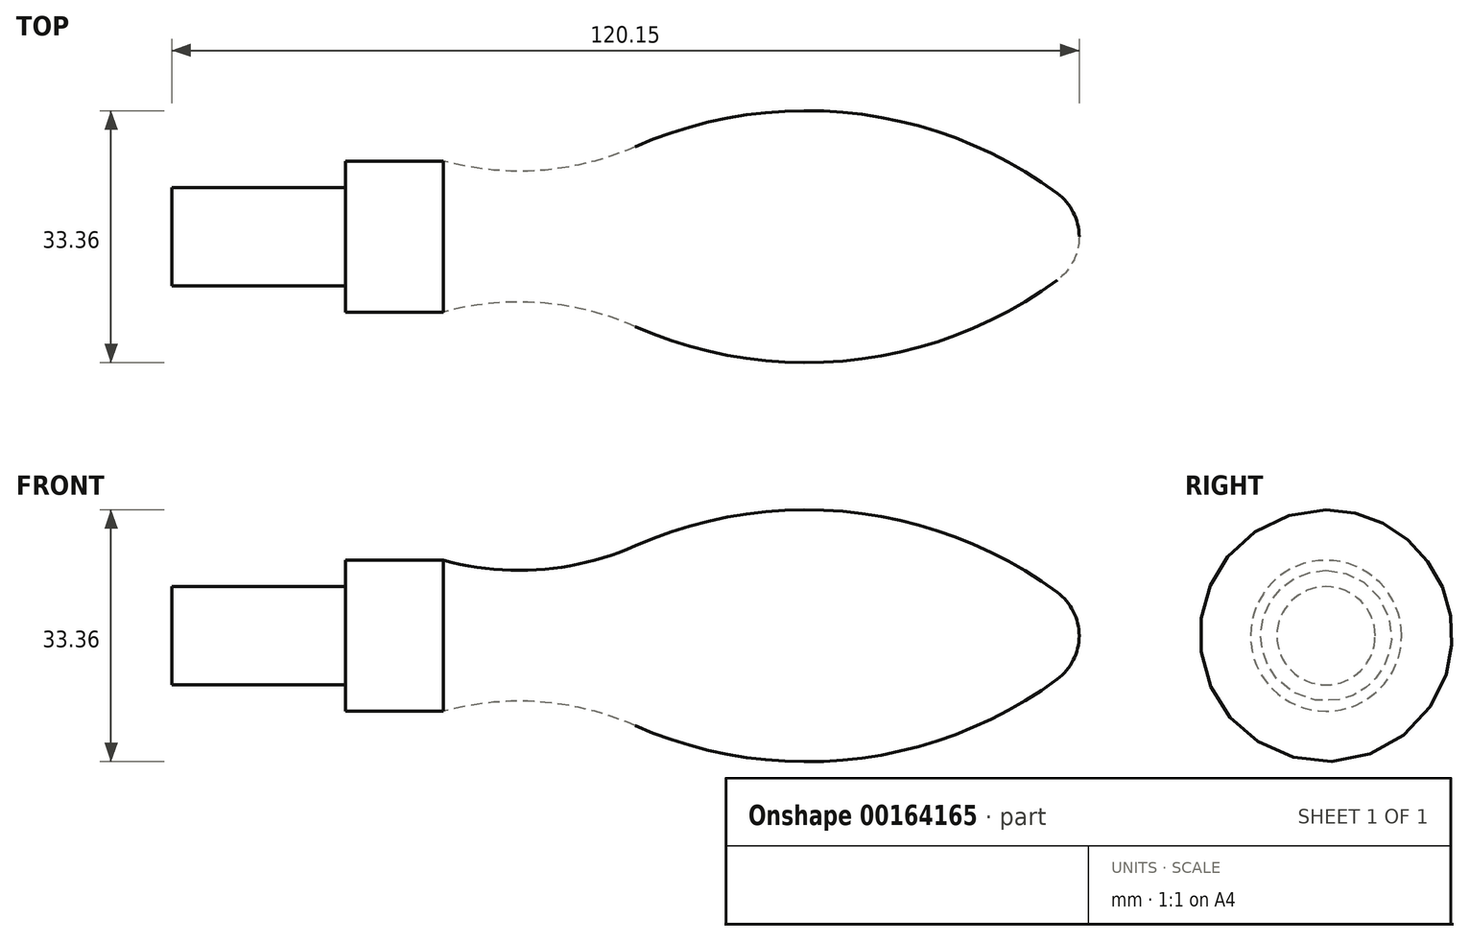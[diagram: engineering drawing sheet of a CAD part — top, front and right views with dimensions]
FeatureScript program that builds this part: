
annotation { "Feature Type Name" : "Feature", "Feature Type Description" : "" }
export const myFeature = defineFeature(function(context is Context, id is Id, definition is map)
    precondition{}
    {
        {
            var Q0;
            Q0=qCreatedBy(makeId("Top.planeOp"),FACE);
            var sketch = newSketch(context, id + "F0", { "sketchPlane" : qUnion([Q0])});
            skLineSegment(sketch, "E0", {"start": v(0, 0) * mm, "end": v(0, 6.5) * mm});
            skLineSegment(sketch, "E1", {"start": v(0, 6.5) * mm, "end": v(23, 6.5) * mm});
            skLineSegment(sketch, "E2", {"start": v(23, 6.5) * mm, "end": v(23, 10) * mm});
            skLineSegment(sketch, "E3", {"start": v(23, 10) * mm, "end": v(36, 10) * mm});
            skArc(sketch, "E4", {"start": v(36, 10) * mm, "mid": v(48.84, 8.77) * mm, "end": v(61.36, 11.9) * mm});
            skArc(sketch, "E5", {"start": v(117.24, 5.75) * mm, "mid": v(90.13, 16.35) * mm, "end": v(61.36, 11.9) * mm});
            skArc(sketch, "E6", {"start": v(120.15, 0) * mm, "mid": v(119.38, 3.22) * mm, "end": v(117.24, 5.75) * mm});
            skLineSegment(sketch, "E7", {"start": v(0, 0) * mm, "end": v(120.15, 0) * mm, "construction": true});
            skLineSegment(sketch, "E8", {"start": v(0, 0) * mm, "end": v(120.15, 0) * mm});
            skSolve(sketch);
        }
        {
            var Q0;
            Q0=makeQuery(id+"F0.imprint","IMPRINT",FACE,{"disambiguationData":[TD([[makeQuery(id+"F0.imprint","IMPRINT",EDGE,{"derivedFrom":sQuery(id+"F0.wireOp",EDGE,"E0")}),-1.0]])]});
            var Q1;
            Q1=sQuery(id+"F0.wireOp",EDGE,"E8");
            revolve(context, id + "F1", {"entities" : qUnion([Q0]), "axis" : qUnion([Q1]), "revolveType" : RevolveType.FULL});
        }
    });
